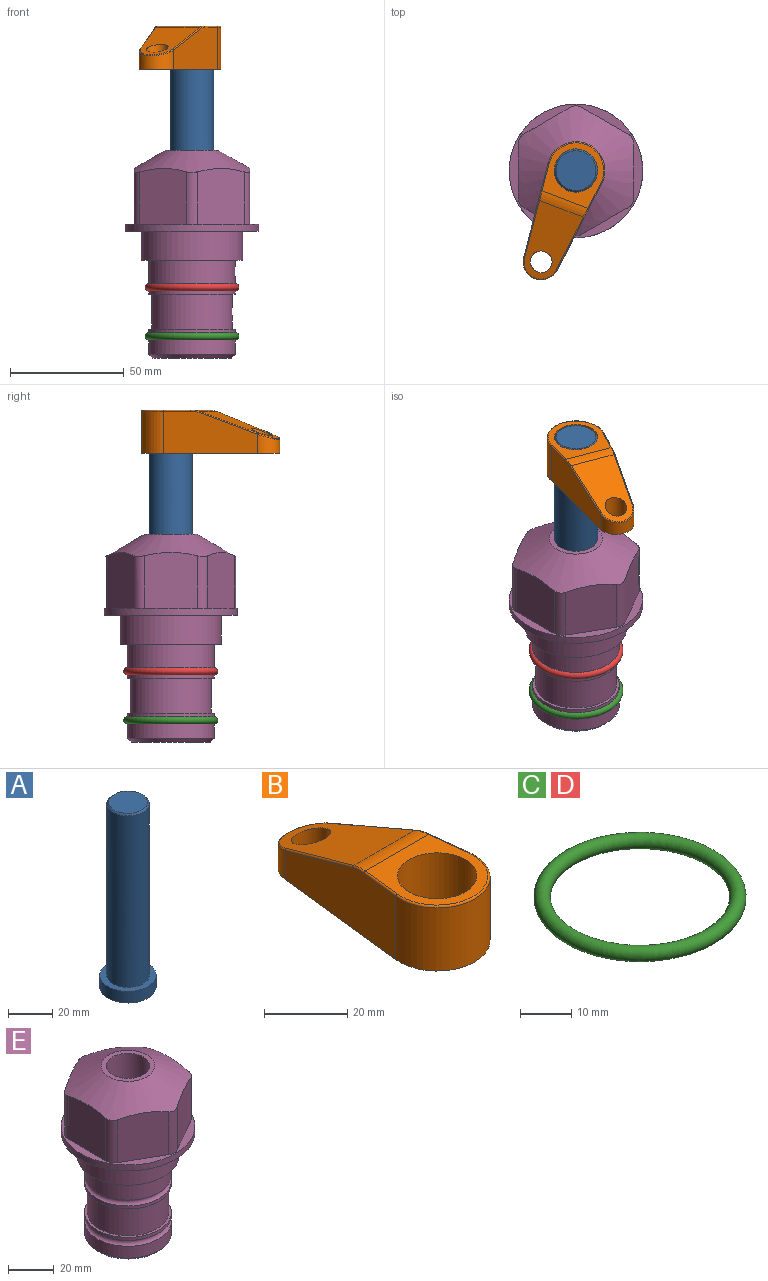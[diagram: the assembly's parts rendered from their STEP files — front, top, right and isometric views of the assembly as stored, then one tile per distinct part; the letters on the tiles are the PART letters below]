
ASSEMBLY  parts=5 mates=3
PART A: 6 faces, bbox 25.4x25.4x101.6 mm
  f0: plane 17.46x17.46mm, normal (0,0,1), area 239.5mm2, adj f5
  f1: plane 25.4x25.4mm, normal (0,0,-1), area 506.7mm2, adj f2
  f2: cylinder r=12.7mm len=25.4mm, axis (0,0,1), area 506.7mm2, adj f1,f3
  f3: plane 25.4x25.4mm, normal (0,0,1), area 221.7mm2, adj f2,f4
  f4: cylinder r=9.53mm len=94.46mm, axis (0,0,1), area 5653mm2, adj f3,f5
  f5: cone r=8.73mm half-angle=45deg, axis (0,0,-1), area 64.4mm2, adj f0,f4
PART B: 44 faces, bbox 27.5x64.5x19.1 mm
  f0: plane 2.3x0.95mm, normal (0,0,-1), area 1mm2, adj f25,f30,f34
  f1: plane 63.5x25.4mm, normal (0,0,-1), area 561.7mm2, adj f2,f3,f4,f5,f6,f7,f19,f20
  f2: cylinder r=12.7mm len=25.4mm, axis (0,0,-1), area 792.2mm2, adj f1,f3,f5,f13
  f3: plane 42.33x18.54mm, normal (0.99,0.11,0), area 647mm2, adj f1,f2,f4,f11,f12,f14
  f4: cylinder r=7.94mm len=15.78mm, axis (0,0,-1), area 158.6mm2, adj f1,f3,f5,f16
  f5: plane 42.33x18.54mm, normal (-0.99,0.11,0), area 647mm2, adj f1,f2,f4,f15,f17,f18
  f6: cylinder r=9.53mm len=19.05mm, axis (0,0,-1), area 1140.1mm2, adj f1,f8
  f7: cylinder r=4.76mm len=10.98mm, axis (0,0,-1), area 276.1mm2, adj f1,f9
  f8: plane 25.83x24.38mm, normal (0,0,1), area 262.2mm2, adj f6,f10,f11,f13,f15
  f9: plane 32.49x20.55mm, normal (0,0.34,0.94), area 489.9mm2, adj f7,f10,f14,f16,f18
  f10: cylinder r=12.7mm len=21.49mm, axis (-1,0,0), area 93.2mm2, adj f8,f9,f12,f17
  f11: cylinder r=0.51mm len=12.34mm, axis (0.11,-0.99,0), area 9.9mm2, adj f3,f8,f12,f13
  f12: bspline ~7.62x1.64mm, area 3.5mm2, adj f3,f10,f11,f14
  f13: torus R=12.19mm, axis (0,0,1), area 33.6mm2, adj f2,f8,f11,f15
  f14: cylinder r=0.51mm len=26.01mm, axis (0.1,-0.93,0.34), area 21.6mm2, adj f3,f9,f12,f16
  f15: cylinder r=0.51mm len=12.34mm, axis (0.11,0.99,0), area 9.9mm2, adj f5,f8,f13,f17
  f16: bspline ~15.78x7.05mm, area 15.7mm2, adj f4,f9,f14,f18
  f17: bspline ~7.62x1.64mm, area 3.5mm2, adj f5,f10,f15,f18
  f18: cylinder r=0.51mm len=26.01mm, axis (0.1,0.93,-0.34), area 21.6mm2, adj f5,f9,f16,f17
  f19: plane 21.6x14.29mm, normal (-0.99,-0.11,0), area 242.6mm2, adj f1,f26,f28,f34,f36,f38
  f20: plane 21.6x14.29mm, normal (0.99,-0.11,0), area 242.6mm2, adj f1,f27,f29,f37,f39,f41
  f21: cylinder r=12.7mm len=14.29mm, axis (0,0,-1), area 173.2mm2, adj f1,f26,f27,f30,f31,f33
  f22: cylinder r=7.94mm len=7.63mm, axis (0,0,-1), area 53.8mm2, adj f1,f28,f29,f42
  f23: plane 2.3x0.95mm, normal (0,0,-1), area 1mm2, adj f25,f33,f37
  f24: plane 17.94x12.32mm, normal (0,-0.34,-0.94), area 191.2mm2, adj f25,f38,f41,f42
  f25: cylinder r=9.53mm len=12.93mm, axis (-1,0,0), area 37.5mm2, adj f0,f23,f24,f31,f36,f39
  f26: cylinder r=1.59mm len=14.29mm, axis (0,0,-1), area 49mm2, adj f1,f19,f21,f32
  f27: cylinder r=1.59mm len=14.29mm, axis (0,0,-1), area 49mm2, adj f1,f20,f21,f35
  f28: cylinder r=1.59mm len=7.28mm, axis (0,0,-1), area 22.1mm2, adj f1,f19,f22,f40
  f29: cylinder r=1.59mm len=7.28mm, axis (0,0,-1), area 22.1mm2, adj f1,f20,f22,f43
  f30: torus R=14.29mm, axis (0,0,1), area 5.8mm2, adj f0,f21,f31,f32
  f31: bspline ~11.06x2.73mm, area 20.8mm2, adj f21,f25,f30,f33
  f32: sphere r=1.59mm, area 5.4mm2, adj f26,f30,f34
  f33: torus R=14.29mm, axis (0,0,1), area 5.8mm2, adj f21,f23,f31,f35
  f34: cylinder r=1.59mm len=1.68mm, axis (-0.11,0.99,0), area 2.4mm2, adj f0,f19,f32,f36
  f35: sphere r=1.59mm, area 5.4mm2, adj f27,f33,f37
  f36: bspline ~5.82x2.33mm, area 7.7mm2, adj f19,f25,f34,f38
  f37: cylinder r=1.59mm len=1.68mm, axis (0.11,0.99,0), area 2.4mm2, adj f20,f23,f35,f39
  f38: cylinder r=1.59mm len=18.33mm, axis (0.1,-0.93,0.34), area 46.7mm2, adj f19,f24,f36,f40
  f39: bspline ~5.82x2.33mm, area 7.7mm2, adj f20,f25,f37,f41
  f40: sphere r=1.59mm, area 3.6mm2, adj f28,f38,f42
  f41: cylinder r=1.59mm len=18.33mm, axis (0.1,0.93,-0.34), area 46.7mm2, adj f20,f24,f39,f43
  f42: bspline ~8.31x1.84mm, area 15.3mm2, adj f22,f24,f40,f43
  f43: sphere r=1.59mm, area 3.6mm2, adj f29,f41,f42
PART C: 1 faces, bbox 44.7x44.7x3.2 mm
  f0: torus R=19.05mm, axis (0,0,1), area 1193.9mm2
PART D: same geometry as C
PART E: 36 faces, bbox 58.7x58.7x91.2 mm
  f0: cylinder r=17.78mm len=35.56mm, axis (0,0,1), area 1670.8mm2, adj f23,f24,f31
  f1: cylinder r=19.05mm len=38.1mm, axis (0,0,1), area 1191.9mm2, adj f26,f27,f30
  f2: plane 58.66x58.66mm, normal (0,0,-1), area 1150.6mm2, adj f3,f28
  f3: cylinder r=29.33mm len=58.66mm, axis (0,0,-1), area 585.1mm2, adj f2,f4
  f4: plane 58.66x58.66mm, normal (0,0,1), area 475.9mm2, adj f3,f5,f6,f7,f8,f9,f10,f11
  f5: plane 24.5x20.32mm, normal (-0.5,0.87,0), area 562.8mm2, adj f4,f15,f16,f17
  f6: plane 24.5x20.32mm, normal (0.5,0.87,0), area 562.8mm2, adj f4,f14,f15,f17
  f7: plane 24.5x23.48mm, normal (1,0,0), area 562.8mm2, adj f4,f13,f14,f17
  f8: plane 24.5x20.32mm, normal (0.5,-0.87,0), area 562.8mm2, adj f4,f12,f13,f17
  f9: plane 24.5x20.32mm, normal (-0.5,-0.87,0), area 562.8mm2, adj f4,f11,f12,f17
  f10: plane 24.5x23.48mm, normal (-1,0,0), area 562.8mm2, adj f4,f11,f16,f17
  f11: cylinder r=5.08mm len=23.01mm, axis (0,0,-1), area 121.2mm2, adj f4,f9,f10,f17
  f12: cylinder r=5.08mm len=23.01mm, axis (0,0,-1), area 121.2mm2, adj f4,f8,f9,f17
  f13: cylinder r=5.08mm len=23.01mm, axis (0,0,-1), area 121.2mm2, adj f4,f7,f8,f17
  f14: cylinder r=5.08mm len=23.01mm, axis (0,0,-1), area 121.2mm2, adj f4,f6,f7,f17
  f15: cylinder r=5.08mm len=23.01mm, axis (0,0,-1), area 121.2mm2, adj f4,f5,f6,f17
  f16: cylinder r=5.08mm len=23.01mm, axis (0,0,-1), area 121.2mm2, adj f4,f5,f10,f17
  f17: cone r=11.73mm half-angle=60deg, axis (0,0,-1), area 2071.8mm2, adj f5,f6,f7,f8,f9,f10,f11,f12
  f18: plane 23.46x23.46mm, normal (0,0,1), area 147.4mm2, adj f17,f35
  f19: plane 34.93x34.93mm, normal (0,0,-1), area 958mm2, adj f29
  f20: cylinder r=19.05mm len=38.1mm, axis (0,0,1), area 760.1mm2, adj f21,f29
  f21: torus R=19.05mm, axis (0,0,1), area 565.3mm2, adj f20,f22
  f22: cylinder r=19.05mm len=38.1mm, axis (0,0,1), area 190mm2, adj f21,f23
  f23: plane 38.1x38.1mm, normal (0,0,1), area 146.9mm2, adj f0,f22
  f24: plane 38.1x38.1mm, normal (0,0,-1), area 146.9mm2, adj f0,f25
  f25: cylinder r=19.05mm len=38.1mm, axis (0,0,1), area 190mm2, adj f24,f26
  f26: torus R=19.05mm, axis (0,0,1), area 565.3mm2, adj f1,f25
  f27: plane 44.45x44.45mm, normal (0,0,-1), area 411.7mm2, adj f1,f28
  f28: cylinder r=22.23mm len=44.45mm, axis (0,0,1), area 1773.5mm2, adj f2,f27
  f29: cone r=19.05mm half-angle=45deg, axis (0,0,1), area 257.5mm2, adj f19,f20
  f30: cylinder r=3.17mm len=6.75mm, axis (-1,0,0), area 128mm2, adj f1,f33
  f31: cylinder r=3.17mm len=6.35mm, axis (-1,0,0), area 102.5mm2, adj f0,f33
  f32: plane 25.4x25.4mm, normal (0,0,1), area 506.7mm2, adj f33
  f33: cylinder r=12.7mm len=66.42mm, axis (0,0,-1), area 5236.2mm2, adj f30,f31,f32,f34
  f34: cone r=9.53mm half-angle=30deg, axis (0,0,-1), area 443.4mm2, adj f33,f35
  f35: cylinder r=9.53mm len=19.05mm, axis (0,0,-1), area 849mm2, adj f18,f34
PLACE A rot(axis=(0,0,-1),110.9deg) t=(0,0,16.57)mm
PLACE B rot(axis=(0,0,1),159.1deg) t=(0,0,71.18)mm
PLACE C t=(0,0,-21.59)mm
PLACE D at identity
PLACE E at identity fixed
MATE fastened C.f0 <-> E.f0  axis (0,0,1) through (0,0,-46.1)mm
MATE cylindrical A.f2 <-> E.f0  axis (0,0,1) through (0,0,42.21)mm
MATE fastened B.f2 <-> A.f2  axis (0,0,1) through (0,0,90.23)mm
